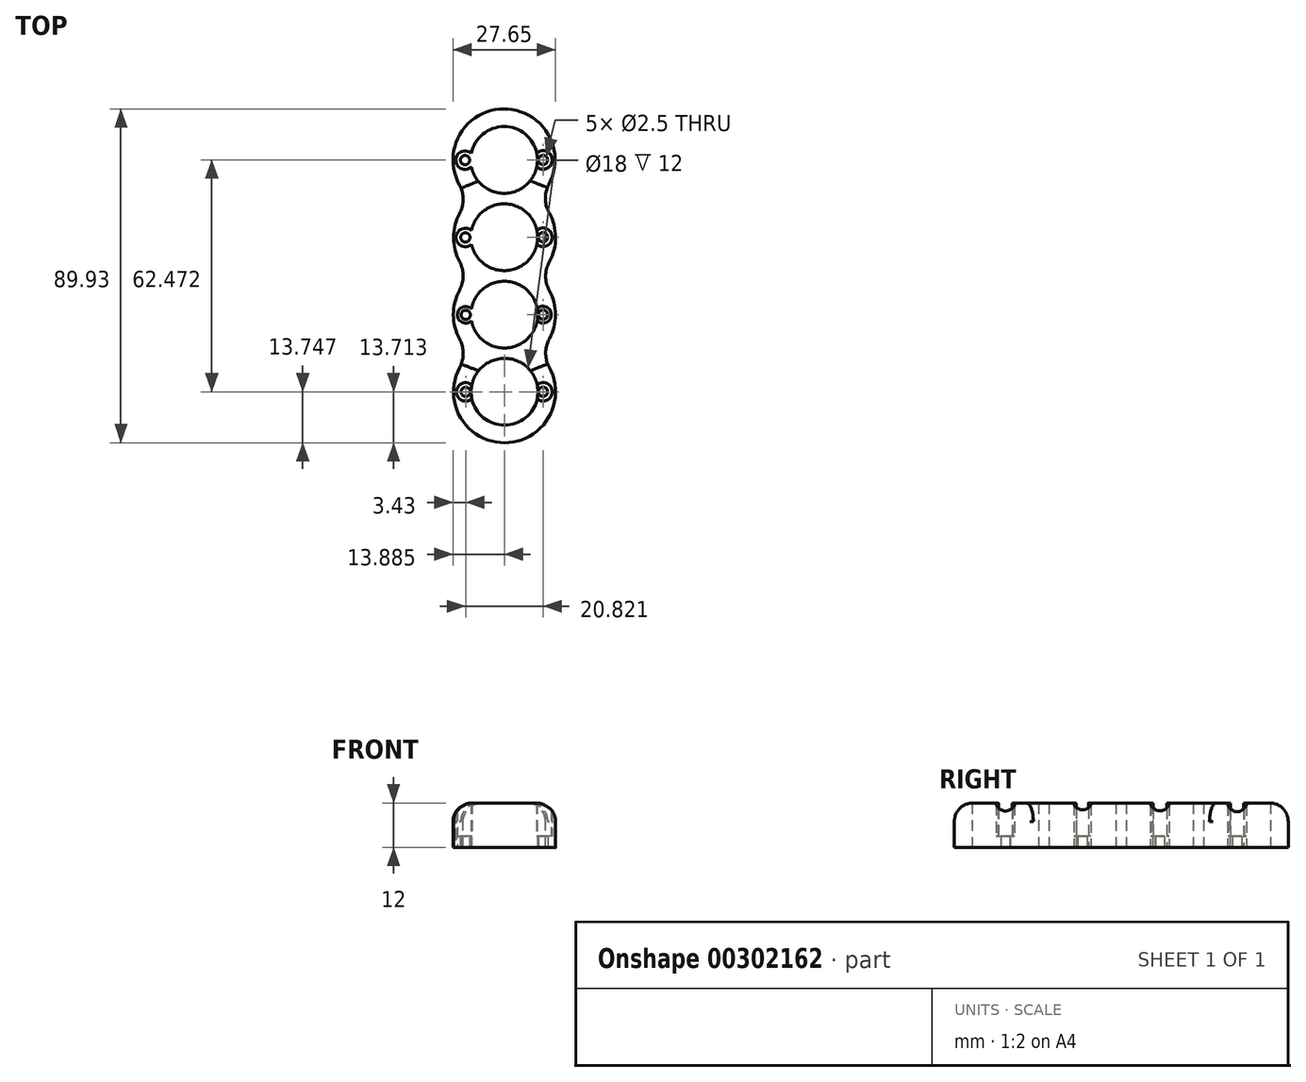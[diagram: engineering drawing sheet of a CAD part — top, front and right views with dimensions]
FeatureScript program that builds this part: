
annotation { "Feature Type Name" : "Feature", "Feature Type Description" : "" }
export const myFeature = defineFeature(function(context is Context, id is Id, definition is map)
    precondition{}
    {
        {
            var Q0;
            Q0=qCreatedBy(makeId("Top.planeOp"),FACE);
            var sketch = newSketch(context, id + "F0", { "sketchPlane" : qUnion([Q0])});
            skLineSegment(sketch, "E0", {"start": v(-16.59, 32.24) * mm, "end": v(-16.41, -49.38) * mm, "construction": true});
            skCircle(sketch, "E1", {"center": v(-16.47, -23.15) * mm, "radius": 9 * mm});
            skCircle(sketch, "E2", {"center": v(-16.51, -2.3) * mm, "radius": 9 * mm});
            skCircle(sketch, "E3", {"center": v(-16.56, 18.51) * mm, "radius": 9 * mm});
            skPoint(sketch, "E4.oppositeSnap0", {"position": v(-7.5, -35.15) * mm});
            skPoint(sketch, "E5.endSnap0", {"position": v(-29.5, -35.15) * mm});
            skCircle(sketch, "E6", {"center": v(-6.06, 18.51) * mm, "radius": 1.25 * mm});
            skCircle(sketch, "E7", {"center": v(-6.06, -2.3) * mm, "radius": 1.25 * mm});
            skCircle(sketch, "E8", {"center": v(-6.06, -23.15) * mm, "radius": 1.25 * mm});
            skCircle(sketch, "E9.MirrorC", {"center": v(-27.06, 18.47) * mm, "radius": 1.25 * mm});
            skCircle(sketch, "E10.MirrorC", {"center": v(-26.97, -2.35) * mm, "radius": 1.25 * mm});
            skCircle(sketch, "E11.MirrorC", {"center": v(-26.88, -23.2) * mm, "radius": 1.25 * mm});
            skCircle(sketch, "E12", {"center": v(-6.06, -43.91) * mm, "radius": 1.25 * mm});
            skCircle(sketch, "E13", {"center": v(-26.88, -43.96) * mm, "radius": 1.25 * mm});
            skCircle(sketch, "E14", {"center": v(-16.43, -43.92) * mm, "radius": 9 * mm});
            skLineSegment(sketch, "E15", {"start": v(-16.51, -2.3) * mm, "end": v(-39.55, -2.35) * mm, "construction": true});
            skLineSegment(sketch, "E16", {"start": v(-16.47, -23.15) * mm, "end": v(-37.2, -23.2) * mm, "construction": true});
            skLineSegment(sketch, "E17", {"start": v(-3.61, -22.63) * mm, "end": v(-3.61, -23.37) * mm});
            skLineSegment(sketch, "E18", {"start": v(-29.44, -22.8) * mm, "end": v(-29.44, -23.31) * mm});
            skLineSegment(sketch, "E19", {"start": v(-29.78, -2.22) * mm, "end": v(-29.77, -2.45) * mm});
            skLineSegment(sketch, "E20", {"start": v(-3.22, -2.2) * mm, "end": v(-3.22, -2.36) * mm});
            skCircle(sketch, "E21", {"center": v(-26.88, -23.2) * mm, "radius": 2.25 * mm});
            skCircle(sketch, "E22", {"center": v(-6.06, -23.15) * mm, "radius": 2.25 * mm});
            skPoint(sketch, "E23.startSnap0", {"position": v(-25.4, -12.84) * mm});
            skPoint(sketch, "E23.endSnap0", {"position": v(-25.36, -33.47) * mm});
            skPoint(sketch, "E24.startSnap0", {"position": v(-25.45, 8.1) * mm});
            skCircle(sketch, "E25", {"center": v(-16.56, 18.51) * mm, "radius": 13.75 * mm});
            skCircle(sketch, "E26", {"center": v(-16.43, -43.92) * mm, "radius": 13.75 * mm});
            skCircle(sketch, "E27", {"center": v(-26.97, -2.35) * mm, "radius": 2.5 * mm});
            skCircle(sketch, "E28", {"center": v(-6.06, -2.3) * mm, "radius": 2.5 * mm});
            skCircle(sketch, "E29", {"center": v(-6.06, 18.51) * mm, "radius": 2.5 * mm});
            skCircle(sketch, "E30", {"center": v(-27.06, 18.47) * mm, "radius": 2.5 * mm});
            skCircle(sketch, "E31", {"center": v(-26.88, -43.96) * mm, "radius": 2.5 * mm});
            skCircle(sketch, "E32", {"center": v(-6.06, -43.91) * mm, "radius": 2.5 * mm});
            skCircle(sketch, "E33", {"center": v(-16.47, -23.15) * mm, "radius": 13.75 * mm});
            skCircle(sketch, "E34", {"center": v(-16.41, -2.37) * mm, "radius": 13.75 * mm});
            skLineSegment(sketch, "E35", {"start": v(49.11, 32.22) * mm, "end": v(49.27, -49.4) * mm, "construction": true});
            skCircle(sketch, "E36", {"center": v(49.22, -23.1) * mm, "radius": 4.7 * mm});
            skCircle(sketch, "E37", {"center": v(49.18, -2.3) * mm, "radius": 4.7 * mm});
            skCircle(sketch, "E38", {"center": v(49.14, 18.5) * mm, "radius": 4.7 * mm});
            skLineSegment(sketch, "E39.bottom", {"start": v(53.97, -27.85) * mm, "end": v(44.47, -27.85) * mm});
            skLineSegment(sketch, "E39.top", {"start": v(53.97, -18.35) * mm, "end": v(44.47, -18.35) * mm});
            skLineSegment(sketch, "E39.left", {"start": v(53.97, -27.85) * mm, "end": v(53.97, -18.35) * mm});
            skLineSegment(sketch, "E39.right", {"start": v(44.47, -27.85) * mm, "end": v(44.47, -18.35) * mm});
            skLineSegment(sketch, "E40.bottom", {"start": v(53.93, -7.05) * mm, "end": v(44.43, -7.05) * mm});
            skLineSegment(sketch, "E40.top", {"start": v(53.93, 2.45) * mm, "end": v(44.43, 2.45) * mm});
            skLineSegment(sketch, "E40.left", {"start": v(53.93, -7.05) * mm, "end": v(53.93, 2.45) * mm});
            skLineSegment(sketch, "E40.right", {"start": v(44.43, -7.05) * mm, "end": v(44.43, 2.45) * mm});
            skLineSegment(sketch, "E41.bottom", {"start": v(53.89, 13.75) * mm, "end": v(44.39, 13.75) * mm});
            skLineSegment(sketch, "E41.top", {"start": v(53.89, 23.25) * mm, "end": v(44.39, 23.25) * mm});
            skLineSegment(sketch, "E41.left", {"start": v(53.89, 13.75) * mm, "end": v(53.89, 23.25) * mm});
            skLineSegment(sketch, "E41.right", {"start": v(44.39, 13.75) * mm, "end": v(44.39, 23.25) * mm});
            skLineSegment(sketch, "E42.bottom", {"start": v(41.14, 13.75) * mm, "end": v(57.14, 13.75) * mm});
            skLineSegment(sketch, "E42.top", {"start": v(41.14, 4.25) * mm, "end": v(57.14, 4.25) * mm});
            skLineSegment(sketch, "E42.left", {"start": v(41.14, 13.75) * mm, "end": v(41.14, 4.25) * mm});
            skLineSegment(sketch, "E42.right", {"start": v(57.14, 13.75) * mm, "end": v(57.14, 4.25) * mm});
            skLineSegment(sketch, "E43.bottom", {"start": v(41.14, -7.05) * mm, "end": v(57.14, -7.05) * mm});
            skLineSegment(sketch, "E43.top", {"start": v(41.14, -16.55) * mm, "end": v(57.14, -16.55) * mm});
            skLineSegment(sketch, "E43.left", {"start": v(41.14, -7.05) * mm, "end": v(41.14, -16.55) * mm});
            skLineSegment(sketch, "E43.right", {"start": v(57.14, -7.05) * mm, "end": v(57.14, -16.55) * mm});
            skPoint(sketch, "E44.oppositeSnap0", {"position": v(58.18, -35.25) * mm});
            skLineSegment(sketch, "E44.bottom", {"start": v(41.14, -27.85) * mm, "end": v(57.14, -27.85) * mm});
            skLineSegment(sketch, "E44.top", {"start": v(41.14, -35.25) * mm, "end": v(57.14, -35.25) * mm});
            skLineSegment(sketch, "E44.left", {"start": v(41.14, -27.85) * mm, "end": v(41.14, -35.25) * mm});
            skLineSegment(sketch, "E44.right", {"start": v(57.14, -27.85) * mm, "end": v(57.14, -35.25) * mm});
            skCircle(sketch, "E45", {"center": v(59.64, 18.5) * mm, "radius": 0.82 * mm});
            skCircle(sketch, "E46", {"center": v(59.64, -2.3) * mm, "radius": 0.82 * mm});
            skCircle(sketch, "E47", {"center": v(59.64, -23.1) * mm, "radius": 0.82 * mm});
            skCircle(sketch, "E48.MirrorC", {"center": v(38.64, 18.46) * mm, "radius": 0.82 * mm});
            skCircle(sketch, "E49.MirrorC", {"center": v(38.72, -2.34) * mm, "radius": 0.82 * mm});
            skCircle(sketch, "E50.MirrorC", {"center": v(38.8, -23.14) * mm, "radius": 0.82 * mm});
            skLineSegment(sketch, "E51.bottom", {"start": v(41.14, -48.65) * mm, "end": v(57.14, -48.65) * mm});
            skLineSegment(sketch, "E51.top", {"start": v(41.14, -57.65) * mm, "end": v(57.14, -57.65) * mm});
            skLineSegment(sketch, "E51.left", {"start": v(41.14, -48.65) * mm, "end": v(41.14, -57.65) * mm});
            skLineSegment(sketch, "E51.right", {"start": v(57.14, -48.65) * mm, "end": v(57.14, -57.65) * mm});
            skLineSegment(sketch, "E52", {"start": v(44.47, -39.17) * mm, "end": v(44.49, -48.65) * mm});
            skCircle(sketch, "E53", {"center": v(59.64, -43.9) * mm, "radius": 0.82 * mm});
            skCircle(sketch, "E54", {"center": v(38.8, -43.9) * mm, "radius": 0.82 * mm});
            skLineSegment(sketch, "E55", {"start": v(44.47, -39.17) * mm, "end": v(53.97, -39.15) * mm});
            skLineSegment(sketch, "E56", {"start": v(53.97, -39.15) * mm, "end": v(53.97, -48.65) * mm});
            skCircle(sketch, "E57", {"center": v(49.26, -43.94) * mm, "radius": 4.7 * mm});
            skSolve(sketch);
        }
        {
            var Q0;
            {var subQ0=sQuery(id+"F0.wireOp",EDGE,"E26");var subQ1=sQuery(id+"F0.wireOp",EDGE,"E1");var subQ2=makeQuery(id+"F0.imprint","INTERSECT",VERTEX,{"disambiguationData":[OD(0.0)],"derivedFrom":[subQ1,subQ0]});Q0=makeQuery(id+"F0.imprint","IMPRINT",FACE,{"disambiguationData":[TD([[makeQuery(id+"F0.imprint","IMPRINT",EDGE,{"disambiguationData":[TD([[subQ2,-1.0]])],"derivedFrom":subQ1}),-1.0]])]});}
            var Q1;
            {var subQ0=sQuery(id+"F0.wireOp",EDGE,"E25");var subQ1=sQuery(id+"F0.wireOp",EDGE,"E2");var subQ2=makeQuery(id+"F0.imprint","INTERSECT",VERTEX,{"disambiguationData":[OD(0.0)],"derivedFrom":[subQ1,subQ0]});Q1=makeQuery(id+"F0.imprint","IMPRINT",FACE,{"disambiguationData":[TD([[makeQuery(id+"F0.imprint","IMPRINT",EDGE,{"disambiguationData":[TD([[subQ2,-1.0]])],"derivedFrom":subQ1}),-1.0]])]});}
            var Q2;
            {var subQ0=sQuery(id+"F0.wireOp",EDGE,"E34");var subQ7=sQuery(id+"F0.wireOp",EDGE,"E1");var subQ8=makeQuery(id+"F0.imprint","INTERSECT",VERTEX,{"disambiguationData":[OD(0.0)],"derivedFrom":[subQ7,subQ0]});Q2=makeQuery(id+"F0.imprint","IMPRINT",FACE,{"disambiguationData":[TD([[makeQuery(id+"F0.imprint","IMPRINT",EDGE,{"disambiguationData":[TD([[subQ8,-1.0]])],"derivedFrom":subQ7}),-1.0]])]});}
            var Q3;
            {var subQ1=sQuery(id+"F0.wireOp",EDGE,"E2");var subQ5=sQuery(id+"F0.wireOp",EDGE,"E25");var subQ7=makeQuery(id+"F0.imprint","INTERSECT",VERTEX,{"disambiguationData":[OD(0.0)],"derivedFrom":[subQ1,subQ5]});Q3=makeQuery(id+"F0.imprint","IMPRINT",FACE,{"disambiguationData":[TD([[makeQuery(id+"F0.imprint","IMPRINT",EDGE,{"disambiguationData":[TD([[subQ7,1.0]])],"derivedFrom":subQ1}),-1.0]])]});}
            var Q4;
            {var subQ1=sQuery(id+"F0.wireOp",EDGE,"E2");var subQ7=sQuery(id+"F0.wireOp",EDGE,"E25");var subQ9=makeQuery(id+"F0.imprint","INTERSECT",VERTEX,{"disambiguationData":[OD(1.0)],"derivedFrom":[subQ1,subQ7]});Q4=makeQuery(id+"F0.imprint","IMPRINT",FACE,{"disambiguationData":[TD([[makeQuery(id+"F0.imprint","IMPRINT",EDGE,{"disambiguationData":[TD([[subQ9,-1.0]])],"derivedFrom":subQ1}),-1.0]])]});}
            var Q5;
            {var subQ3=sQuery(id+"F0.wireOp",EDGE,"E1");var subQ5=sQuery(id+"F0.wireOp",EDGE,"E34");var subQ6=makeQuery(id+"F0.imprint","INTERSECT",VERTEX,{"disambiguationData":[OD(1.0)],"derivedFrom":[subQ3,subQ5]});Q5=makeQuery(id+"F0.imprint","IMPRINT",FACE,{"disambiguationData":[TD([[makeQuery(id+"F0.imprint","IMPRINT",EDGE,{"disambiguationData":[TD([[subQ6,-1.0]])],"derivedFrom":subQ3}),-1.0]])]});}
            var Q6;
            {var subQ3=sQuery(id+"F0.wireOp",EDGE,"E1");var subQ5=sQuery(id+"F0.wireOp",EDGE,"E34");var subQ6=makeQuery(id+"F0.imprint","INTERSECT",VERTEX,{"disambiguationData":[OD(0.0)],"derivedFrom":[subQ3,subQ5]});Q6=makeQuery(id+"F0.imprint","IMPRINT",FACE,{"disambiguationData":[TD([[makeQuery(id+"F0.imprint","IMPRINT",EDGE,{"disambiguationData":[TD([[subQ6,1.0]])],"derivedFrom":subQ3}),-1.0]])]});}
            var Q7;
            {var subQ1=sQuery(id+"F0.wireOp",EDGE,"E14");var subQ6=sQuery(id+"F0.wireOp",EDGE,"E33");var subQ11=makeQuery(id+"F0.imprint","INTERSECT",VERTEX,{"disambiguationData":[OD(0.0)],"derivedFrom":[subQ1,subQ6]});Q7=makeQuery(id+"F0.imprint","IMPRINT",FACE,{"disambiguationData":[TD([[makeQuery(id+"F0.imprint","IMPRINT",EDGE,{"disambiguationData":[TD([[subQ11,1.0]])],"derivedFrom":subQ1}),-1.0]])]});}
            var Q8;
            {var subQ1=sQuery(id+"F0.wireOp",EDGE,"E3");var subQ9=sQuery(id+"F0.wireOp",EDGE,"E30");var subQ10=makeQuery(id+"F0.imprint","INTERSECT",VERTEX,{"disambiguationData":[OD(0.0)],"derivedFrom":[subQ1,subQ9]});Q8=makeQuery(id+"F0.imprint","IMPRINT",FACE,{"disambiguationData":[TD([[makeQuery(id+"F0.imprint","IMPRINT",EDGE,{"disambiguationData":[TD([[subQ10,1.0]])],"derivedFrom":subQ1}),-1.0]])]});}
            extrude(context, id + "F1", {"entities" : qUnion([Q0, Q1, Q2, Q3, Q4, Q5, Q6, Q7, Q8]), "depth" : 12 * mm});
        }
        {
            var Q0;
            Q0=makeQuery(id+"F0.imprint","IMPRINT",FACE,{"disambiguationData":[TD([[makeQuery(id+"F0.imprint","IMPRINT",EDGE,{"derivedFrom":sQuery(id+"F0.wireOp",EDGE,"E8")}),-1.0]])]});
            var Q1;
            {var subQ0=sQuery(id+"F0.wireOp",EDGE,"E21");var subQ1=sQuery(id+"F0.wireOp",EDGE,"073f5de2-028e-462f-9cef-9b1b6fd825d90.MirrorCS");var subQ2=makeQuery(id+"F0.imprint","INTERSECT",VERTEX,{"disambiguationData":[OD(0.0)],"derivedFrom":[subQ1,subQ0]});Q1=makeQuery(id+"F0.imprint","IMPRINT",FACE,{"disambiguationData":[TD([[makeQuery(id+"F0.imprint","IMPRINT",EDGE,{"disambiguationData":[TD([[subQ2,-1.0]])],"derivedFrom":subQ1}),-1.0]])]});}
            var Q2;
            Q2=makeQuery(id+"F0.imprint","IMPRINT",FACE,{"disambiguationData":[TD([[makeQuery(id+"F0.imprint","IMPRINT",EDGE,{"derivedFrom":sQuery(id+"F0.wireOp",EDGE,"E11.MirrorC")}),1.0]])]});
            var Q3;
            {var subQ0=sQuery(id+"F0.wireOp",EDGE,"E21");var subQ1=sQuery(id+"F0.wireOp",EDGE,"d793a48b-257a-4737-bc45-a45dbda491930.MirrorCS");var subQ2=makeQuery(id+"F0.imprint","INTERSECT",VERTEX,{"disambiguationData":[OD(0.0)],"derivedFrom":[subQ1,subQ0]});Q3=makeQuery(id+"F0.imprint","IMPRINT",FACE,{"disambiguationData":[TD([[makeQuery(id+"F0.imprint","IMPRINT",EDGE,{"disambiguationData":[TD([[subQ2,-1.0]])],"derivedFrom":subQ1}),1.0]])]});}
            var Q4;
            {var subQ0=sQuery(id+"F0.wireOp",EDGE,"E22");var subQ1=sQuery(id+"F0.wireOp",EDGE,"3404ae05-0c8b-4081-b07d-0651607c9c130.MirrorCS");var subQ2=makeQuery(id+"F0.imprint","INTERSECT",VERTEX,{"disambiguationData":[OD(0.0)],"derivedFrom":[subQ1,subQ0]});Q4=makeQuery(id+"F0.imprint","IMPRINT",FACE,{"disambiguationData":[TD([[makeQuery(id+"F0.imprint","IMPRINT",EDGE,{"disambiguationData":[TD([[subQ2,-1.0]])],"derivedFrom":subQ1}),-1.0]])]});}
            var Q5;
            {var subQ0=sQuery(id+"F0.wireOp",EDGE,"E22");var subQ1=sQuery(id+"F0.wireOp",EDGE,"kTRhAb7x-PPG7-BJcY-bXVo-2Zxu0mkdpO8j");var subQ2=makeQuery(id+"F0.imprint","INTERSECT",VERTEX,{"disambiguationData":[OD(0.0)],"derivedFrom":[subQ1,subQ0]});Q5=makeQuery(id+"F0.imprint","IMPRINT",FACE,{"disambiguationData":[TD([[makeQuery(id+"F0.imprint","IMPRINT",EDGE,{"disambiguationData":[TD([[subQ2,-1.0]])],"derivedFrom":subQ1}),1.0]])]});}
            var Q6;
            Q6=makeQuery(id+"F0.imprint","IMPRINT",FACE,{"disambiguationData":[TD([[makeQuery(id+"F0.imprint","IMPRINT",EDGE,{"derivedFrom":sQuery(id+"F0.wireOp",EDGE,"E10.MirrorC")}),1.0]])]});
            var Q7;
            Q7=makeQuery(id+"F0.imprint","IMPRINT",FACE,{"disambiguationData":[TD([[makeQuery(id+"F0.imprint","IMPRINT",EDGE,{"derivedFrom":sQuery(id+"F0.wireOp",EDGE,"E7")}),-1.0]])]});
            var Q8;
            Q8=makeQuery(id+"F0.imprint","IMPRINT",FACE,{"disambiguationData":[TD([[makeQuery(id+"F0.imprint","IMPRINT",EDGE,{"derivedFrom":sQuery(id+"F0.wireOp",EDGE,"E6")}),-1.0]])]});
            var Q9;
            Q9=makeQuery(id+"F0.imprint","IMPRINT",FACE,{"disambiguationData":[TD([[makeQuery(id+"F0.imprint","IMPRINT",EDGE,{"derivedFrom":sQuery(id+"F0.wireOp",EDGE,"E9.MirrorC")}),1.0]])]});
            var Q10;
            Q10=makeQuery(id+"F0.imprint","IMPRINT",FACE,{"disambiguationData":[TD([[makeQuery(id+"F0.imprint","IMPRINT",EDGE,{"derivedFrom":sQuery(id+"F0.wireOp",EDGE,"E13")}),-1.0]])]});
            var Q11;
            Q11=makeQuery(id+"F0.imprint","IMPRINT",FACE,{"disambiguationData":[TD([[makeQuery(id+"F0.imprint","IMPRINT",EDGE,{"derivedFrom":sQuery(id+"F0.wireOp",EDGE,"E12")}),-1.0]])]});
            extrude(context, id + "F2", {"entities" : qUnion([Q0, Q1, Q2, Q3, Q4, Q5, Q6, Q7, Q8, Q9, Q10, Q11]), "operationType" : NewBodyOperationType.ADD, "depth" : 3 * mm});
        }
        {
            var Q0;
            {var subQ0=sQuery(id+"F0.wireOp",EDGE,"E33");var subQ1=sQuery(id+"F0.wireOp",EDGE,"E26");Q0=makeQuery(id+"F1.opExtrude","SWEPT_EDGE",EDGE,{"disambiguationData":[OSD([subQ1,subQ0]),TDD([makeQuery(id+"F0.imprint","INTERSECT",VERTEX,{"disambiguationData":[OD(0.0)],"derivedFrom":[subQ1,subQ0]})])]});}
            var Q1;
            {var subQ0=sQuery(id+"F0.wireOp",EDGE,"E34");var subQ1=sQuery(id+"F0.wireOp",EDGE,"E33");Q1=makeQuery(id+"F1.opExtrude","SWEPT_EDGE",EDGE,{"disambiguationData":[OSD([subQ1,subQ0]),TDD([makeQuery(id+"F0.imprint","INTERSECT",VERTEX,{"disambiguationData":[OD(0.0)],"derivedFrom":[subQ1,subQ0]})])]});}
            var Q2;
            {var subQ0=sQuery(id+"F0.wireOp",EDGE,"E34");var subQ1=sQuery(id+"F0.wireOp",EDGE,"E25");Q2=makeQuery(id+"F1.opExtrude","SWEPT_EDGE",EDGE,{"disambiguationData":[OSD([subQ1,subQ0]),TDD([makeQuery(id+"F0.imprint","INTERSECT",VERTEX,{"disambiguationData":[OD(1.0)],"derivedFrom":[subQ1,subQ0]})])]});}
            var Q3;
            {var subQ0=sQuery(id+"F0.wireOp",EDGE,"E34");var subQ1=sQuery(id+"F0.wireOp",EDGE,"E25");Q3=makeQuery(id+"F1.opExtrude","SWEPT_EDGE",EDGE,{"disambiguationData":[OSD([subQ1,subQ0]),TDD([makeQuery(id+"F0.imprint","INTERSECT",VERTEX,{"disambiguationData":[OD(0.0)],"derivedFrom":[subQ1,subQ0]})])]});}
            var Q4;
            {var subQ0=sQuery(id+"F0.wireOp",EDGE,"E34");var subQ1=sQuery(id+"F0.wireOp",EDGE,"E33");Q4=makeQuery(id+"F1.opExtrude","SWEPT_EDGE",EDGE,{"disambiguationData":[OSD([subQ1,subQ0]),TDD([makeQuery(id+"F0.imprint","INTERSECT",VERTEX,{"disambiguationData":[OD(1.0)],"derivedFrom":[subQ1,subQ0]})])]});}
            var Q5;
            {var subQ0=sQuery(id+"F0.wireOp",EDGE,"E33");var subQ1=sQuery(id+"F0.wireOp",EDGE,"E26");Q5=makeQuery(id+"F1.opExtrude","SWEPT_EDGE",EDGE,{"disambiguationData":[OSD([subQ1,subQ0]),TDD([makeQuery(id+"F0.imprint","INTERSECT",VERTEX,{"disambiguationData":[OD(1.0)],"derivedFrom":[subQ1,subQ0]})])]});}
            fillet(context, id + "F3", {"entities" : qUnion([Q0, Q1, Q2, Q3, Q4, Q5]), "radius" : 8 * mm, "tangentPropagation" : true, "allowEdgeOverflow" : false});
        }
        {
            var Q0;
            Q0=makeQuery(id+"F1.opExtrude","CAP_EDGE",EDGE,{"disambiguationData":[OSD([sQuery(id+"F0.wireOp",EDGE,"E26")])],"isStart":false});
            fillet(context, id + "F4", {"entities" : qUnion([Q0]), "radius" : 5 * mm, "tangentPropagation" : true, "allowEdgeOverflow" : false});
        }
    });
